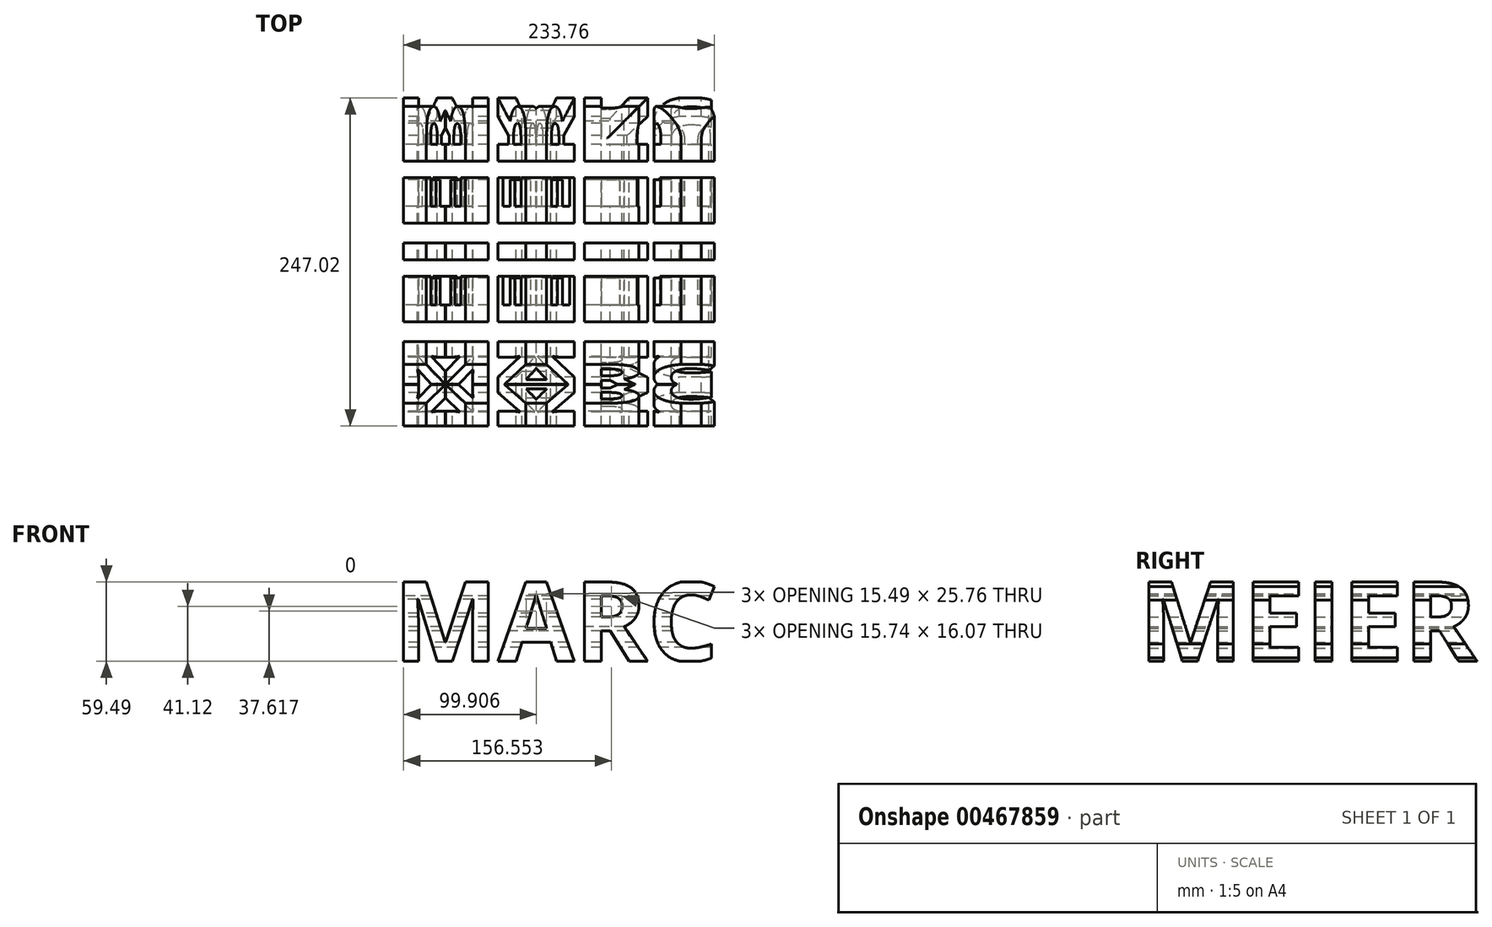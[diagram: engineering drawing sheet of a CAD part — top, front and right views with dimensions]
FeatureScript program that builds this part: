
annotation { "Feature Type Name" : "Feature", "Feature Type Description" : "" }
export const myFeature = defineFeature(function(context is Context, id is Id, definition is map)
    precondition{}
    {
        {
            var Q0;
            Q0=qCreatedBy(makeId("Front.planeOp"),FACE);
            var sketch = newSketch(context, id + "F0", { "sketchPlane" : qUnion([Q0])});
            skText(sketch, "E0", { "text": "MARC", "fontName": "OpenSans-Bold.ttf"});
            skLineSegment(sketch, "E1", {"start": v(-123.33, 0) * mm, "end": v(123.33, 0) * mm, "construction": true});
            const initialGuessF0  = {"E0": [-0.12333, -0.03, 1, 0, 0.06]};
            skSetInitialGuess(sketch, initialGuessF0);
            skSolve(sketch);
        }
        {
            var Q0;
            Q0 = qSketchRegion(id + "F0", true);
            extrude(context, id + "F1", {"entities" : qUnion([Q0]), "endBound" : BoundingType.SYMMETRIC, "offsetDistance" : 25 * mm, "depth" : 400 * mm});
        }
        {
            var Q0;
            Q0=qCreatedBy(makeId("Right.planeOp"),FACE);
            var sketch = newSketch(context, id + "F2", { "sketchPlane" : qUnion([Q0])});
            skText(sketch, "E2", { "text": "MEIER", "fontName": "OpenSans-Bold.ttf"});
            skLineSegment(sketch, "E3", {"start": v(-129.95, 0) * mm, "end": v(129.95, 0) * mm, "construction": true});
            const initialGuessF2  = {"E2": [-0.12995, -0.03, 1, 0, 0.06]};
            skSetInitialGuess(sketch, initialGuessF2);
            skSolve(sketch);
        }
        {
            var Q0;
            Q0 = qSketchRegion(id + "F2", true);
            extrude(context, id + "F3", {"entities" : qUnion([Q0]), "operationType" : NewBodyOperationType.INTERSECT, "endBound" : BoundingType.SYMMETRIC, "offsetDistance" : 25 * mm, "depth" : 500 * mm});
        }
    });
